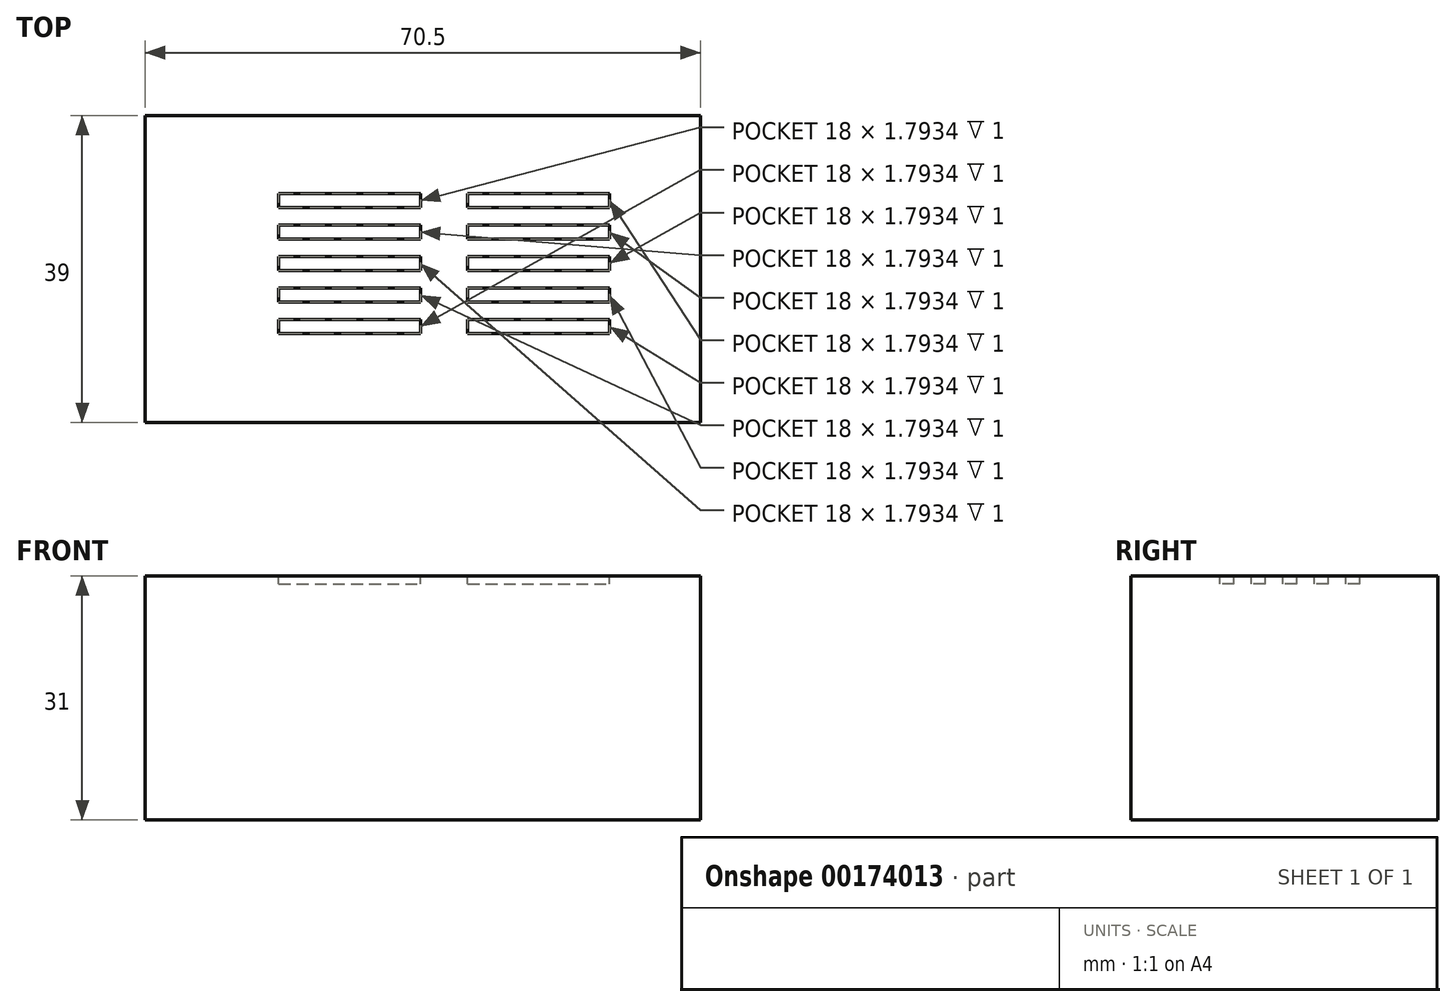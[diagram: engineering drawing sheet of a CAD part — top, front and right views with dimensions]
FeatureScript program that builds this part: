
annotation { "Feature Type Name" : "Feature", "Feature Type Description" : "" }
export const myFeature = defineFeature(function(context is Context, id is Id, definition is map)
    precondition{}
    {
        {
            var Q0;
            Q0=qCreatedBy(makeId("Top.planeOp"),FACE);
            var sketch = newSketch(context, id + "F0", { "sketchPlane" : qUnion([Q0])});
            skLineSegment(sketch, "E0.bottom", {"start": v(35.25, 19.5) * mm, "end": v(-35.25, 19.5) * mm});
            skLineSegment(sketch, "E0.top", {"start": v(35.25, -19.5) * mm, "end": v(-35.25, -19.5) * mm});
            skLineSegment(sketch, "E0.left", {"start": v(35.25, 19.5) * mm, "end": v(35.25, -19.5) * mm});
            skLineSegment(sketch, "E0.right", {"start": v(-35.25, 19.5) * mm, "end": v(-35.25, -19.5) * mm});
            skPoint(sketch, "E0.middle", {"position": v(0, 0) * mm});
            skSolve(sketch);
        }
        {
            var Q0;
            Q0 = qSketchRegion(id + "F0", true);
            extrude(context, id + "F1", {"entities" : qUnion([Q0]), "depth" : 31 * mm});
        }
        {
            var Q0;
            Q0=makeQuery(id+"F1.opExtrude","CAP_FACE",FACE,{"disambiguationData":[OSD([sQuery(id+"F0.wireOp",EDGE,"E0.bottom"),sQuery(id+"F0.wireOp",EDGE,"E0.top"),sQuery(id+"F0.wireOp",EDGE,"E0.left"),sQuery(id+"F0.wireOp",EDGE,"E0.right")])],"isStart":false});
            var sketch = newSketch(context, id + "F2", { "sketchPlane" : qUnion([Q0])});
            skPoint(sketch, "E1.centerSnap0", {"position": v(-35.25, 0) * mm});
            skLineSegment(sketch, "E2.bottom", {"start": v(-18.3, 9.6) * mm, "end": v(-0.3, 9.6) * mm});
            skLineSegment(sketch, "E2.top", {"start": v(-18.3, 7.81) * mm, "end": v(-0.3, 7.81) * mm});
            skLineSegment(sketch, "E2.left", {"start": v(-18.3, 9.6) * mm, "end": v(-18.3, 7.81) * mm});
            skLineSegment(sketch, "E2.right", {"start": v(-0.3, 9.6) * mm, "end": v(-0.3, 7.81) * mm});
            skLineSegment(sketch, "E3.bottom", {"start": v(5.7, 9.6) * mm, "end": v(23.7, 9.6) * mm});
            skLineSegment(sketch, "E3.top", {"start": v(5.7, 7.81) * mm, "end": v(23.7, 7.81) * mm});
            skLineSegment(sketch, "E3.left", {"start": v(5.7, 9.6) * mm, "end": v(5.7, 7.81) * mm});
            skLineSegment(sketch, "E3.right", {"start": v(23.7, 9.6) * mm, "end": v(23.7, 7.81) * mm});
            skLineSegment(sketch, "E4.1.0.0", {"start": v(23.7, 5.6) * mm, "end": v(23.7, 3.81) * mm});
            skLineSegment(sketch, "E4.1.0.1", {"start": v(-18.3, 5.6) * mm, "end": v(-0.3, 5.6) * mm});
            skLineSegment(sketch, "E4.1.0.2", {"start": v(5.7, 3.81) * mm, "end": v(23.7, 3.81) * mm});
            skLineSegment(sketch, "E4.1.0.3", {"start": v(-18.3, 5.6) * mm, "end": v(-18.3, 3.81) * mm});
            skLineSegment(sketch, "E4.1.0.4", {"start": v(5.7, 5.6) * mm, "end": v(5.7, 3.81) * mm});
            skLineSegment(sketch, "E4.1.0.5", {"start": v(5.7, 5.6) * mm, "end": v(23.7, 5.6) * mm});
            skLineSegment(sketch, "E4.1.0.6", {"start": v(-0.3, 5.6) * mm, "end": v(-0.3, 3.81) * mm});
            skLineSegment(sketch, "E4.1.0.7", {"start": v(-18.3, 3.81) * mm, "end": v(-0.3, 3.81) * mm});
            skLineSegment(sketch, "E4.2.0.0", {"start": v(23.7, 1.6) * mm, "end": v(23.7, -0.19) * mm});
            skLineSegment(sketch, "E4.2.0.1", {"start": v(-18.3, 1.6) * mm, "end": v(-0.3, 1.6) * mm});
            skLineSegment(sketch, "E4.2.0.2", {"start": v(5.7, -0.19) * mm, "end": v(23.7, -0.19) * mm});
            skLineSegment(sketch, "E4.2.0.3", {"start": v(-18.3, 1.6) * mm, "end": v(-18.3, -0.19) * mm});
            skLineSegment(sketch, "E4.2.0.4", {"start": v(5.7, 1.6) * mm, "end": v(5.7, -0.19) * mm});
            skLineSegment(sketch, "E4.2.0.5", {"start": v(5.7, 1.6) * mm, "end": v(23.7, 1.6) * mm});
            skLineSegment(sketch, "E4.2.0.6", {"start": v(-0.3, 1.6) * mm, "end": v(-0.3, -0.19) * mm});
            skLineSegment(sketch, "E4.2.0.7", {"start": v(-18.3, -0.19) * mm, "end": v(-0.3, -0.19) * mm});
            skLineSegment(sketch, "E4.3.0.0", {"start": v(23.7, -2.4) * mm, "end": v(23.7, -4.19) * mm});
            skLineSegment(sketch, "E4.3.0.1", {"start": v(-18.3, -2.4) * mm, "end": v(-0.3, -2.4) * mm});
            skLineSegment(sketch, "E4.3.0.2", {"start": v(5.7, -4.19) * mm, "end": v(23.7, -4.19) * mm});
            skLineSegment(sketch, "E4.3.0.3", {"start": v(-18.3, -2.4) * mm, "end": v(-18.3, -4.19) * mm});
            skLineSegment(sketch, "E4.3.0.4", {"start": v(5.7, -2.4) * mm, "end": v(5.7, -4.19) * mm});
            skLineSegment(sketch, "E4.3.0.5", {"start": v(5.7, -2.4) * mm, "end": v(23.7, -2.4) * mm});
            skLineSegment(sketch, "E4.3.0.6", {"start": v(-0.3, -2.4) * mm, "end": v(-0.3, -4.19) * mm});
            skLineSegment(sketch, "E4.3.0.7", {"start": v(-18.3, -4.19) * mm, "end": v(-0.3, -4.19) * mm});
            skLineSegment(sketch, "E4.4.0.0", {"start": v(23.7, -6.4) * mm, "end": v(23.7, -8.19) * mm});
            skLineSegment(sketch, "E4.4.0.1", {"start": v(-18.3, -6.4) * mm, "end": v(-0.3, -6.4) * mm});
            skLineSegment(sketch, "E4.4.0.2", {"start": v(5.7, -8.19) * mm, "end": v(23.7, -8.19) * mm});
            skLineSegment(sketch, "E4.4.0.3", {"start": v(-18.3, -6.4) * mm, "end": v(-18.3, -8.19) * mm});
            skLineSegment(sketch, "E4.4.0.4", {"start": v(5.7, -6.4) * mm, "end": v(5.7, -8.19) * mm});
            skLineSegment(sketch, "E4.4.0.5", {"start": v(5.7, -6.4) * mm, "end": v(23.7, -6.4) * mm});
            skLineSegment(sketch, "E4.4.0.6", {"start": v(-0.3, -6.4) * mm, "end": v(-0.3, -8.19) * mm});
            skLineSegment(sketch, "E4.4.0.7", {"start": v(-18.3, -8.19) * mm, "end": v(-0.3, -8.19) * mm});
            skLineSegment(sketch, "E4.direction1", {"start": v(-18.3, 7.81) * mm, "end": v(-18.3, 3.81) * mm, "construction": true});
            skSolve(sketch);
        }
        {
            var Q0;
            Q0 = qSketchRegion(id + "F2", true);
            extrude(context, id + "F3", {"entities" : qUnion([Q0]), "operationType" : NewBodyOperationType.REMOVE, "oppositeDirection" : true, "depth" : 1 * mm});
        }
    });
